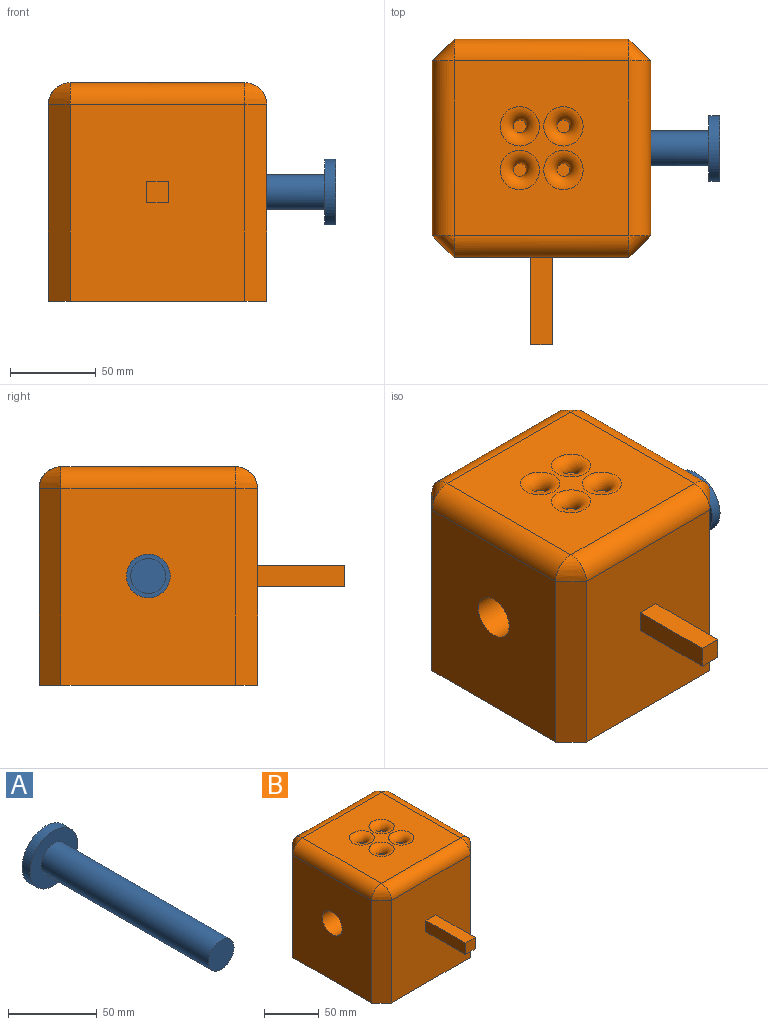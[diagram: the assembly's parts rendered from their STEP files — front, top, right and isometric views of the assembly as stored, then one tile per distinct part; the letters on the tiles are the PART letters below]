
ASSEMBLY  parts=2 mates=1
PART A: 5 faces, bbox 38.1x139.7x38.1 mm
  f0: cylinder r=10.16mm len=133.35mm, axis (0,1,0), area 8512.7mm2, adj f1,f3
  f1: plane 20.32x20.32mm, normal (0,-1,0), area 324.3mm2, adj f0
  f2: cylinder r=19.05mm len=38.1mm, axis (0,1,0), area 760.1mm2, adj f3,f4
  f3: plane 38.1x38.1mm, normal (0,-1,0), area 815.8mm2, adj f0,f2
  f4: plane 38.1x38.1mm, normal (0,1,0), area 1140.1mm2, adj f2
PART B: 32 faces, bbox 128.3x178.4x127 mm
  f0: plane 114.3x101.6mm, normal (0,-1,0), area 11451.6mm2, adj f4,f7,f14,f16,f27,f28,f29,f30
  f1: plane 114.3x101.6mm, normal (1,0,0), area 11106.2mm2, adj f4,f9,f12,f14,f26
  f2: plane 101.6x101.6mm, normal (0,0,1), area 8680.8mm2, adj f6,f7,f8,f9,f22,f23,f24,f25
  f3: plane 114.3x101.6mm, normal (-1,0,0), area 11106.2mm2, adj f4,f6,f10,f16,f26
  f4: plane 127x127mm, normal (0,0,-1), area 15806.4mm2, adj f0,f1,f3,f5,f10,f12,f14,f16
  f5: plane 114.3x101.6mm, normal (0,1,0), area 11612.9mm2, adj f4,f8,f10,f12
  f6: cylinder r=12.7mm len=101.6mm, axis (0,1,0), area 2026.8mm2, adj f2,f3,f11,f17
  f7: cylinder r=12.7mm len=101.6mm, axis (1,0,0), area 2026.8mm2, adj f0,f2,f15,f17
  f8: cylinder r=12.7mm len=101.6mm, axis (-1,0,0), area 2026.8mm2, adj f2,f5,f11,f13
  f9: cylinder r=12.7mm len=101.6mm, axis (0,-1,0), area 2026.8mm2, adj f1,f2,f13,f15
  f10: plane 114.3x12.7mm, normal (-0.71,0.71,0), area 2052.9mm2, adj f3,f4,f5,f11
  f11: bspline ~13.33x13.33mm, area 211.6mm2, adj f6,f8,f10
  f12: plane 114.3x12.7mm, normal (0.71,0.71,0), area 2052.9mm2, adj f1,f4,f5,f13
  f13: bspline ~13.33x13.33mm, area 211.6mm2, adj f8,f9,f12
  f14: plane 114.3x12.7mm, normal (0.71,-0.71,0), area 2052.9mm2, adj f0,f1,f4,f15
  f15: bspline ~13.33x13.33mm, area 211.6mm2, adj f7,f9,f14
  f16: plane 114.3x12.7mm, normal (-0.71,-0.71,0), area 2052.9mm2, adj f0,f3,f4,f17
  f17: bspline ~13.33x13.33mm, area 211.6mm2, adj f6,f7,f16
  f18: plane 7.62x7.62mm, normal (0,0,1), area 45.6mm2, adj f25
  f19: plane 7.62x7.62mm, normal (0,0,1), area 45.6mm2, adj f24
  f20: plane 7.62x7.62mm, normal (0,0,1), area 45.6mm2, adj f23
  f21: plane 7.62x7.62mm, normal (0,0,1), area 45.6mm2, adj f22
  f22: torus R=11.43mm, axis (0,0,-1), area 494.8mm2, adj f2,f21
  f23: torus R=11.43mm, axis (0,0,-1), area 494.8mm2, adj f2,f20
  f24: torus R=11.43mm, axis (0,0,-1), area 494.8mm2, adj f2,f19
  f25: torus R=11.43mm, axis (0,0,-1), area 494.8mm2, adj f2,f18
  f26: cylinder r=12.7mm len=127mm, axis (1,0,0), area 10134.1mm2, adj f1,f3
  f27: plane 50.8x12.7mm, normal (1,0,0), area 645.2mm2, adj f0,f28,f30,f31
  f28: plane 50.8x12.7mm, normal (0,0,1), area 645.2mm2, adj f0,f27,f29,f31
  f29: plane 50.8x12.7mm, normal (-1,0,0), area 645.2mm2, adj f0,f28,f30,f31
  f30: plane 50.8x12.7mm, normal (0,0,-1), area 645.2mm2, adj f0,f27,f29,f31
  f31: plane 12.7x12.7mm, normal (0,-1,0), area 161.3mm2, adj f27,f28,f29,f30
PLACE A rot(axis=(-0.71,-0.71,0),180deg) t=(33.72,-15.07,-19.6)mm
PLACE B t=(0,-15.07,-19.6)mm
MATE cylindrical A.f0 <-> B.f26  axis (-1,0,0) through (-36.13,-15.07,-19.6)mm
